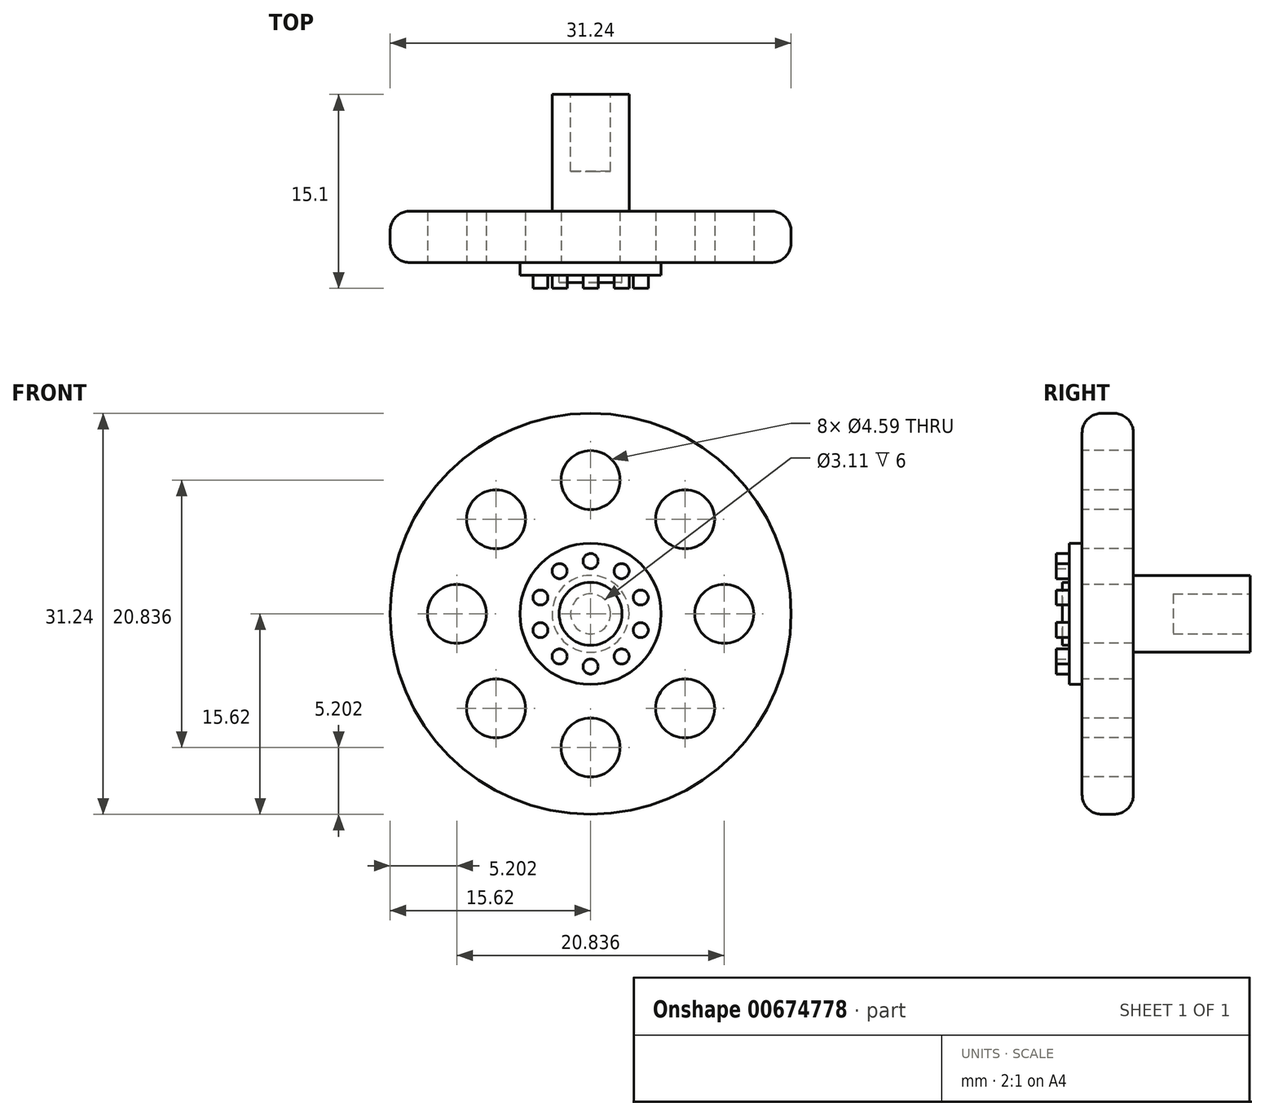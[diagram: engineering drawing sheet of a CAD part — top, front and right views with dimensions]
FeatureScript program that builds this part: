
annotation { "Feature Type Name" : "Feature", "Feature Type Description" : "" }
export const myFeature = defineFeature(function(context is Context, id is Id, definition is map)
    precondition{}
    {
        {
            var Q0;
            Q0=qCreatedBy(makeId("Front.planeOp"),FACE);
            var sketch = newSketch(context, id + "F0", { "sketchPlane" : qUnion([Q0])});
            skCircle(sketch, "E0", {"center": v(0, 0) * mm, "radius": 15.62 * mm});
            skSolve(sketch);
        }
        {
            var Q0;
            Q0=makeQuery(id+"F0.imprint","IMPRINT",FACE,{"disambiguationData":[TD([[makeQuery(id+"F0.imprint","IMPRINT",EDGE,{"derivedFrom":sQuery(id+"F0.wireOp",EDGE,"E0")}),1.0]])]});
            extrude(context, id + "F1", {"entities" : qUnion([Q0]), "depth" : 4 * mm, "offsetDistance" : 25.4 * mm});
        }
        {
            var Q0;
            Q0=makeQuery(id+"F1.opExtrude","CAP_FACE",FACE,{"disambiguationData":[OSD([sQuery(id+"F0.wireOp",EDGE,"E0")])],"isStart":false});
            var sketch = newSketch(context, id + "F2", { "sketchPlane" : qUnion([Q0])});
            skCircle(sketch, "E1", {"center": v(0, 0) * mm, "radius": 2.45 * mm});
            skSolve(sketch);
        }
        {
            var Q0;
            Q0=makeQuery(id+"F2.imprint","IMPRINT",FACE,{"disambiguationData":[TD([[makeQuery(id+"F2.imprint","IMPRINT",EDGE,{"derivedFrom":sQuery(id+"F2.wireOp",EDGE,"E1")}),1.0]])]});
            extrude(context, id + "F3", {"entities" : qUnion([Q0]), "operationType" : NewBodyOperationType.ADD, "depth" : 1.55 * mm, "offsetDistance" : 25.4 * mm});
        }
        {
            var Q0;
            Q0=makeQuery(id+"F0.imprint","IMPRINT",FACE,{"disambiguationData":[TD([[makeQuery(id+"F0.imprint","IMPRINT",EDGE,{"derivedFrom":sQuery(id+"F0.wireOp",EDGE,"E0")}),1.0]])]});
            var sketch = newSketch(context, id + "F4", { "sketchPlane" : qUnion([Q0])});
            skCircle(sketch, "E2", {"center": v(0, 0) * mm, "radius": 3 * mm});
            skSolve(sketch);
        }
        {
            var Q0;
            Q0=makeQuery(id+"F4.imprint","IMPRINT",FACE,{"disambiguationData":[TD([[makeQuery(id+"F4.imprint","IMPRINT",EDGE,{"derivedFrom":sQuery(id+"F4.wireOp",EDGE,"E2")}),1.0]])]});
            extrude(context, id + "F5", {"entities" : qUnion([Q0]), "operationType" : NewBodyOperationType.ADD, "oppositeDirection" : true, "depth" : 9.1 * mm, "offsetDistance" : 25.4 * mm});
        }
        {
            var Q0;
            Q0=makeQuery(id+"F5.opExtrude","CAP_FACE",FACE,{"disambiguationData":[OSD([sQuery(id+"F4.wireOp",EDGE,"E2")])],"isStart":false});
            var sketch = newSketch(context, id + "F6", { "sketchPlane" : qUnion([Q0])});
            skCircle(sketch, "E3", {"center": v(0, 0) * mm, "radius": 1.55 * mm});
            skSolve(sketch);
        }
        {
            var Q0;
            Q0=makeQuery(id+"F6.imprint","IMPRINT",FACE,{"disambiguationData":[TD([[makeQuery(id+"F6.imprint","IMPRINT",EDGE,{"derivedFrom":sQuery(id+"F6.wireOp",EDGE,"E3")}),1.0]])]});
            extrude(context, id + "F7", {"entities" : qUnion([Q0]), "operationType" : NewBodyOperationType.REMOVE, "oppositeDirection" : true, "depth" : 6 * mm, "offsetDistance" : 25.4 * mm});
        }
        {
            var Q0;
            Q0=makeQuery(id+"F1.opExtrude","CAP_FACE",FACE,{"disambiguationData":[OSD([sQuery(id+"F0.wireOp",EDGE,"E0")])],"isStart":false});
            var sketch = newSketch(context, id + "F8", { "sketchPlane" : qUnion([Q0])});
            skCircle(sketch, "E4", {"center": v(0, 0) * mm, "radius": 5.5 * mm});
            skSolve(sketch);
        }
        {
            var Q0;
            Q0=makeQuery(id+"F8.imprint","IMPRINT",FACE,{"disambiguationData":[TD([[makeQuery(id+"F8.imprint","IMPRINT",EDGE,{"derivedFrom":sQuery(id+"F8.wireOp",EDGE,"E4")}),1.0]])]});
            var sketch = newSketch(context, id + "F9", { "sketchPlane" : qUnion([Q0])});
            skSolve(sketch);
        }
        {
            var Q0;
            Q0=makeQuery(id+"F9.imprint","IMPRINT",FACE,{"disambiguationData":[TD([[makeQuery(id+"F9.imprint","IMPRINT",EDGE,{"derivedFrom":makeQuery(id+"F8.imprint","IMPRINT",EDGE,{"derivedFrom":sQuery(id+"F8.wireOp",EDGE,"E4")})}),1.0]])]});
            extrude(context, id + "F10", {"entities" : qUnion([Q0]), "operationType" : NewBodyOperationType.ADD, "depth" : 1 * mm, "offsetDistance" : 25.4 * mm});
        }
        {
            var Q0;
            Q0=makeQuery(id+"F1.opExtrude","CAP_EDGE",EDGE,{"disambiguationData":[OSD([sQuery(id+"F0.wireOp",EDGE,"E0")])],"isStart":false});
            fillet(context, id + "F11", {"entities" : qUnion([Q0]), "radius" : 1.52 * mm, "tangentPropagation" : true, "allowEdgeOverflow" : false});
        }
        {
            var Q0;
            Q0=makeQuery(id+"F1.opExtrude","CAP_EDGE",EDGE,{"disambiguationData":[OSD([sQuery(id+"F0.wireOp",EDGE,"E0")])],"isStart":true});
            fillet(context, id + "F12", {"entities" : qUnion([Q0]), "radius" : 1.52 * mm, "tangentPropagation" : true, "allowEdgeOverflow" : false});
        }
        {
            var Q0;
            Q0=makeQuery(id+"F10.opExtrude","CAP_FACE",FACE,{"disambiguationData":[OSD([sQuery(id+"F2.wireOp",EDGE,"E1"),sQuery(id+"F8.wireOp",EDGE,"E4")])],"isStart":false});
            var sketch = newSketch(context, id + "F13", { "sketchPlane" : qUnion([Q0])});
            skCircle(sketch, "E5", {"center": v(0, 4.1) * mm, "radius": 0.59 * mm});
            skCircle(sketch, "E6.1.0", {"center": v(-2.42, 3.32) * mm, "radius": 0.59 * mm});
            skCircle(sketch, "E6.2.0", {"center": v(-3.9, 1.27) * mm, "radius": 0.59 * mm});
            skCircle(sketch, "E6.3.0", {"center": v(-3.9, -1.27) * mm, "radius": 0.59 * mm});
            skCircle(sketch, "E6.4.0", {"center": v(-2.42, -3.32) * mm, "radius": 0.59 * mm});
            skCircle(sketch, "E6.5.0", {"center": v(0, -4.1) * mm, "radius": 0.59 * mm});
            skCircle(sketch, "E6.6.0", {"center": v(2.42, -3.32) * mm, "radius": 0.59 * mm});
            skCircle(sketch, "E6.7.0", {"center": v(3.9, -1.27) * mm, "radius": 0.59 * mm});
            skCircle(sketch, "E6.8.0", {"center": v(3.9, 1.27) * mm, "radius": 0.59 * mm});
            skCircle(sketch, "E6.9.0", {"center": v(2.42, 3.32) * mm, "radius": 0.59 * mm});
            skPoint(sketch, "E6.center", {"position": v(0, 0) * mm});
            skSolve(sketch);
        }
        {
            var Q0;
            Q0=makeQuery(id+"F13.imprint","IMPRINT",FACE,{"disambiguationData":[TD([[makeQuery(id+"F13.imprint","IMPRINT",EDGE,{"derivedFrom":sQuery(id+"F13.wireOp",EDGE,"E6.7.0")}),1.0]])]});
            var Q1;
            Q1=makeQuery(id+"F13.imprint","IMPRINT",FACE,{"disambiguationData":[TD([[makeQuery(id+"F13.imprint","IMPRINT",EDGE,{"derivedFrom":sQuery(id+"F13.wireOp",EDGE,"E6.5.0")}),1.0]])]});
            var Q2;
            Q2=makeQuery(id+"F13.imprint","IMPRINT",FACE,{"disambiguationData":[TD([[makeQuery(id+"F13.imprint","IMPRINT",EDGE,{"derivedFrom":sQuery(id+"F13.wireOp",EDGE,"E6.3.0")}),1.0]])]});
            var Q3;
            Q3=makeQuery(id+"F13.imprint","IMPRINT",FACE,{"disambiguationData":[TD([[makeQuery(id+"F13.imprint","IMPRINT",EDGE,{"derivedFrom":sQuery(id+"F13.wireOp",EDGE,"E6.4.0")}),1.0]])]});
            var Q4;
            Q4=makeQuery(id+"F13.imprint","IMPRINT",FACE,{"disambiguationData":[TD([[makeQuery(id+"F13.imprint","IMPRINT",EDGE,{"derivedFrom":sQuery(id+"F13.wireOp",EDGE,"E6.2.0")}),1.0]])]});
            var Q5;
            Q5=makeQuery(id+"F13.imprint","IMPRINT",FACE,{"disambiguationData":[TD([[makeQuery(id+"F13.imprint","IMPRINT",EDGE,{"derivedFrom":sQuery(id+"F13.wireOp",EDGE,"E6.1.0")}),1.0]])]});
            var Q6;
            Q6=makeQuery(id+"F13.imprint","IMPRINT",FACE,{"disambiguationData":[TD([[makeQuery(id+"F13.imprint","IMPRINT",EDGE,{"derivedFrom":sQuery(id+"F13.wireOp",EDGE,"E5")}),1.0]])]});
            var Q7;
            Q7=makeQuery(id+"F13.imprint","IMPRINT",FACE,{"disambiguationData":[TD([[makeQuery(id+"F13.imprint","IMPRINT",EDGE,{"derivedFrom":sQuery(id+"F13.wireOp",EDGE,"E6.9.0")}),1.0]])]});
            var Q8;
            Q8=makeQuery(id+"F13.imprint","IMPRINT",FACE,{"disambiguationData":[TD([[makeQuery(id+"F13.imprint","IMPRINT",EDGE,{"derivedFrom":sQuery(id+"F13.wireOp",EDGE,"E6.8.0")}),1.0]])]});
            var Q9;
            Q9=makeQuery(id+"F13.imprint","IMPRINT",FACE,{"disambiguationData":[TD([[makeQuery(id+"F13.imprint","IMPRINT",EDGE,{"derivedFrom":sQuery(id+"F13.wireOp",EDGE,"E6.6.0")}),1.0]])]});
            extrude(context, id + "F14", {"entities" : qUnion([Q0, Q1, Q2, Q3, Q4, Q5, Q6, Q7, Q8, Q9]), "operationType" : NewBodyOperationType.ADD, "depth" : 1 * mm, "offsetDistance" : 25.4 * mm});
        }
        {
            var Q0;
            Q0=makeQuery(id+"F8.imprint","IMPRINT",FACE,{"disambiguationData":[TD([[makeQuery(id+"F8.imprint","IMPRINT",EDGE,{"derivedFrom":sQuery(id+"F8.wireOp",EDGE,"E4")}),-1.0]])]});
            var sketch = newSketch(context, id + "F15", { "sketchPlane" : qUnion([Q0])});
            skCircle(sketch, "E7", {"center": v(0, 10.42) * mm, "radius": 2.3 * mm});
            skCircle(sketch, "E8.1.0", {"center": v(-7.37, 7.37) * mm, "radius": 2.3 * mm});
            skCircle(sketch, "E8.2.0", {"center": v(-10.42, 0) * mm, "radius": 2.3 * mm});
            skCircle(sketch, "E8.3.0", {"center": v(-7.37, -7.37) * mm, "radius": 2.3 * mm});
            skCircle(sketch, "E8.4.0", {"center": v(0, -10.42) * mm, "radius": 2.3 * mm});
            skCircle(sketch, "E8.5.0", {"center": v(7.37, -7.37) * mm, "radius": 2.3 * mm});
            skCircle(sketch, "E8.6.0", {"center": v(10.42, 0) * mm, "radius": 2.3 * mm});
            skCircle(sketch, "E8.7.0", {"center": v(7.37, 7.37) * mm, "radius": 2.3 * mm});
            skPoint(sketch, "E8.center", {"position": v(0, 0) * mm});
            skSolve(sketch);
        }
        {
            var Q0;
            Q0=makeQuery(id+"F15.imprint","IMPRINT",FACE,{"disambiguationData":[TD([[makeQuery(id+"F15.imprint","IMPRINT",EDGE,{"derivedFrom":sQuery(id+"F15.wireOp",EDGE,"E8.7.0")}),1.0]])]});
            var Q1;
            Q1=makeQuery(id+"F15.imprint","IMPRINT",FACE,{"disambiguationData":[TD([[makeQuery(id+"F15.imprint","IMPRINT",EDGE,{"derivedFrom":sQuery(id+"F15.wireOp",EDGE,"E7")}),1.0]])]});
            var Q2;
            Q2=makeQuery(id+"F15.imprint","IMPRINT",FACE,{"disambiguationData":[TD([[makeQuery(id+"F15.imprint","IMPRINT",EDGE,{"derivedFrom":sQuery(id+"F15.wireOp",EDGE,"E8.1.0")}),1.0]])]});
            var Q3;
            Q3=makeQuery(id+"F15.imprint","IMPRINT",FACE,{"disambiguationData":[TD([[makeQuery(id+"F15.imprint","IMPRINT",EDGE,{"derivedFrom":sQuery(id+"F15.wireOp",EDGE,"E8.2.0")}),1.0]])]});
            var Q4;
            Q4=makeQuery(id+"F15.imprint","IMPRINT",FACE,{"disambiguationData":[TD([[makeQuery(id+"F15.imprint","IMPRINT",EDGE,{"derivedFrom":sQuery(id+"F15.wireOp",EDGE,"E8.3.0")}),1.0]])]});
            var Q5;
            Q5=makeQuery(id+"F15.imprint","IMPRINT",FACE,{"disambiguationData":[TD([[makeQuery(id+"F15.imprint","IMPRINT",EDGE,{"derivedFrom":sQuery(id+"F15.wireOp",EDGE,"E8.4.0")}),1.0]])]});
            var Q6;
            Q6=makeQuery(id+"F15.imprint","IMPRINT",FACE,{"disambiguationData":[TD([[makeQuery(id+"F15.imprint","IMPRINT",EDGE,{"derivedFrom":sQuery(id+"F15.wireOp",EDGE,"E8.5.0")}),1.0]])]});
            var Q7;
            Q7=makeQuery(id+"F15.imprint","IMPRINT",FACE,{"disambiguationData":[TD([[makeQuery(id+"F15.imprint","IMPRINT",EDGE,{"derivedFrom":sQuery(id+"F15.wireOp",EDGE,"E8.6.0")}),1.0]])]});
            extrude(context, id + "F16", {"entities" : qUnion([Q0, Q1, Q2, Q3, Q4, Q5, Q6, Q7]), "operationType" : NewBodyOperationType.REMOVE, "oppositeDirection" : true, "depth" : 25.4 * mm, "offsetDistance" : 25.4 * mm});
        }
    });
